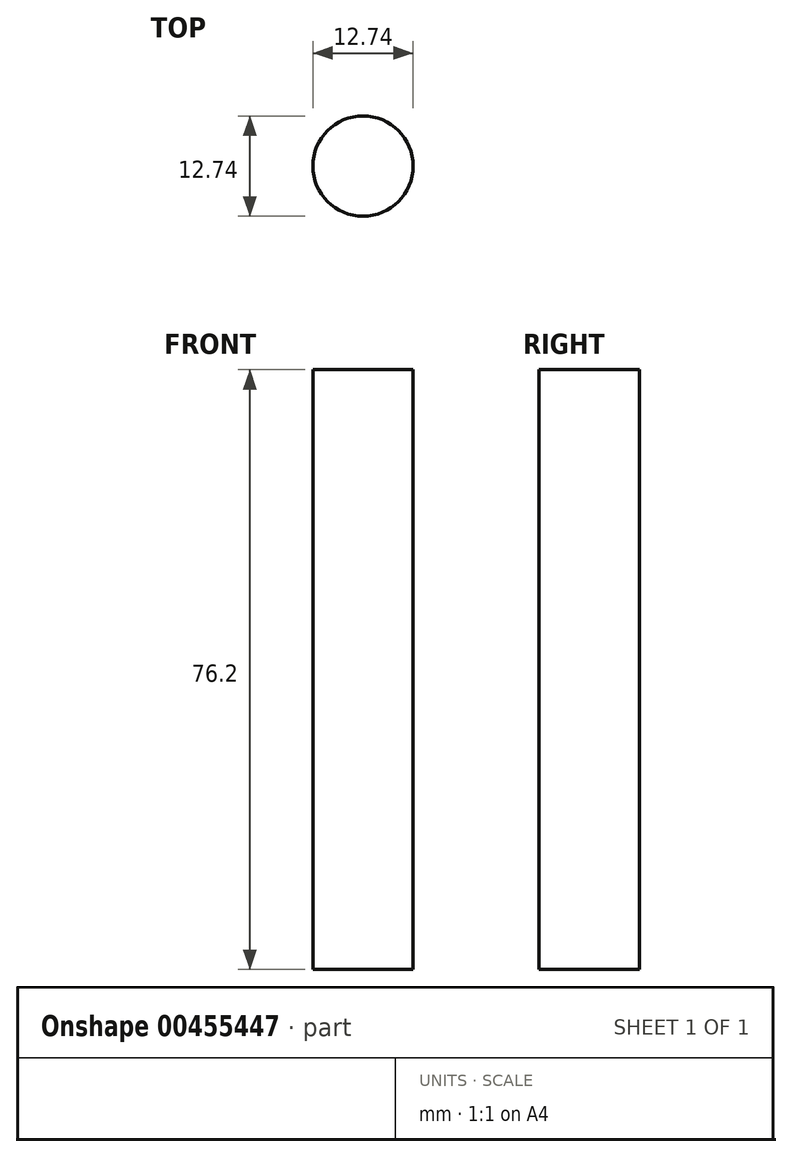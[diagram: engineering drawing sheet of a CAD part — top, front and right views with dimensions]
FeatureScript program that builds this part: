
annotation { "Feature Type Name" : "Feature", "Feature Type Description" : "" }
export const myFeature = defineFeature(function(context is Context, id is Id, definition is map)
    precondition{}
    {
        {
            var Q0;
            Q0=qCreatedBy(makeId("Top.planeOp"),FACE);
            var sketch = newSketch(context, id + "F0", { "sketchPlane" : qUnion([Q0])});
            skCircle(sketch, "E0", {"center": v(0, 0) * mm, "radius": 6.37 * mm});
            skSolve(sketch);
        }
        {
            var Q0;
            Q0=sQuery(id+"F0.wireOp",EDGE,"E0");
            extrude(context, id + "F1", {"bodyType" : ToolBodyType.SURFACE, "surfaceEntities" : qUnion([Q0]), "depth" : 76.2 * mm});
        }
    });
